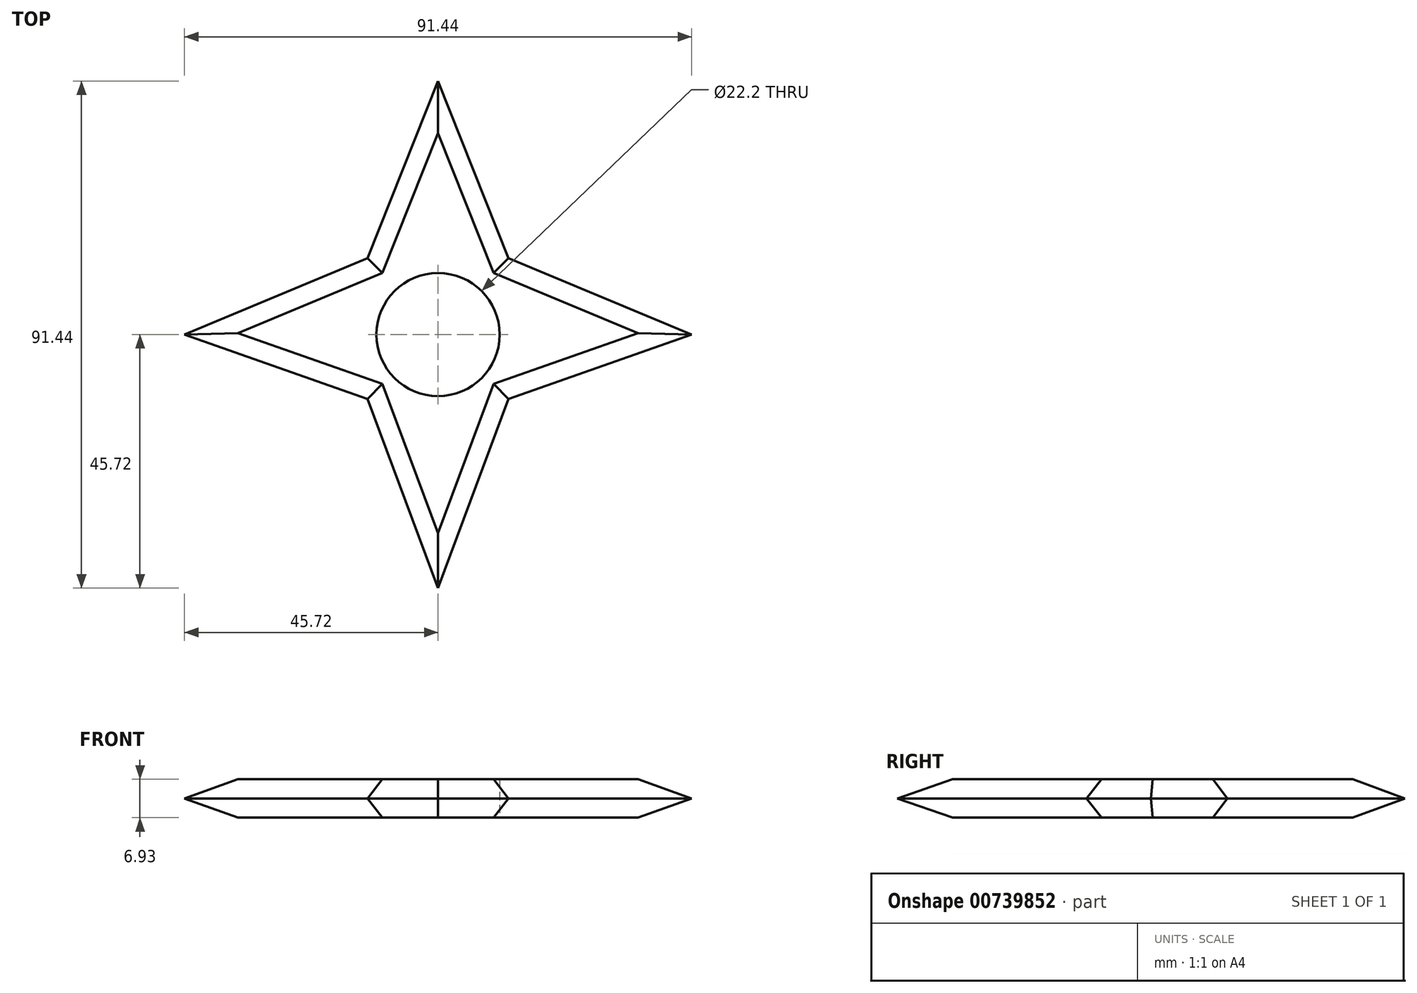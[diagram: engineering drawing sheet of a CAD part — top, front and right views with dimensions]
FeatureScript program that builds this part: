
annotation { "Feature Type Name" : "Feature", "Feature Type Description" : "" }
export const myFeature = defineFeature(function(context is Context, id is Id, definition is map)
    precondition{}
    {
        {
            var Q0;
            Q0=qCreatedBy(makeId("Top.planeOp"),FACE);
            var sketch = newSketch(context, id + "F0", { "sketchPlane" : qUnion([Q0])});
            skCircle(sketch, "E0", {"center": v(0, 0) * mm, "radius": 11.1 * mm});
            skLineSegment(sketch, "E1", {"start": v(0, 45.72) * mm, "end": v(-12.7, 13.75) * mm});
            skLineSegment(sketch, "E2", {"start": v(-12.7, 13.75) * mm, "end": v(-45.72, 0) * mm});
            skLineSegment(sketch, "E3", {"start": v(-45.72, 0) * mm, "end": v(-12.7, -11.65) * mm});
            skLineSegment(sketch, "E4", {"start": v(-12.7, -11.65) * mm, "end": v(0, -45.72) * mm});
            skLineSegment(sketch, "E5", {"start": v(0, -45.72) * mm, "end": v(12.7, -11.65) * mm});
            skLineSegment(sketch, "E6", {"start": v(12.7, -11.65) * mm, "end": v(45.72, 0) * mm});
            skLineSegment(sketch, "E7", {"start": v(45.72, 0) * mm, "end": v(12.7, 13.75) * mm});
            skLineSegment(sketch, "E8", {"start": v(12.7, 13.75) * mm, "end": v(0, 45.72) * mm});
            skSolve(sketch);
        }
        {
            var Q0;
            Q0=makeQuery(id+"F0.imprint","IMPRINT",FACE,{"disambiguationData":[TD([[makeQuery(id+"F0.imprint","IMPRINT",EDGE,{"derivedFrom":sQuery(id+"F0.wireOp",EDGE,"E0")}),-1.0]])]});
            extrude(context, id + "F1", {"entities" : qUnion([Q0]), "depth" : 6.93 * mm, "offsetDistance" : 25.4 * mm});
        }
        {
            var Q0;
            Q0=makeQuery(id+"F1.opExtrude","CAP_EDGE",EDGE,{"disambiguationData":[OSD([sQuery(id+"F0.wireOp",EDGE,"E5")])],"isStart":false});
            var Q1;
            Q1=makeQuery(id+"F1.opExtrude","CAP_EDGE",EDGE,{"disambiguationData":[OSD([sQuery(id+"F0.wireOp",EDGE,"E6")])],"isStart":false});
            var Q2;
            Q2=makeQuery(id+"F1.opExtrude","CAP_EDGE",EDGE,{"disambiguationData":[OSD([sQuery(id+"F0.wireOp",EDGE,"E3")])],"isStart":false});
            var Q3;
            Q3=makeQuery(id+"F1.opExtrude","CAP_EDGE",EDGE,{"disambiguationData":[OSD([sQuery(id+"F0.wireOp",EDGE,"E1")])],"isStart":false});
            var Q4;
            Q4=makeQuery(id+"F1.opExtrude","CAP_EDGE",EDGE,{"disambiguationData":[OSD([sQuery(id+"F0.wireOp",EDGE,"E2")])],"isStart":false});
            var Q5;
            Q5=makeQuery(id+"F1.opExtrude","CAP_EDGE",EDGE,{"disambiguationData":[OSD([sQuery(id+"F0.wireOp",EDGE,"E8")])],"isStart":false});
            var Q6;
            Q6=makeQuery(id+"F1.opExtrude","CAP_EDGE",EDGE,{"disambiguationData":[OSD([sQuery(id+"F0.wireOp",EDGE,"E7")])],"isStart":false});
            var Q7;
            Q7=makeQuery(id+"F1.opExtrude","CAP_EDGE",EDGE,{"disambiguationData":[OSD([sQuery(id+"F0.wireOp",EDGE,"E4")])],"isStart":false});
            chamfer(context, id + "F2", {"entities" : qUnion([Q0, Q1, Q2, Q3, Q4, Q5, Q6, Q7]), "width" : 3.47 * mm, "tangentPropagation" : true});
        }
        {
            var Q0;
            Q0=makeQuery(id+"F1.opExtrude","CAP_EDGE",EDGE,{"disambiguationData":[OSD([sQuery(id+"F0.wireOp",EDGE,"E5")])],"isStart":true});
            var Q1;
            Q1=makeQuery(id+"F1.opExtrude","CAP_EDGE",EDGE,{"disambiguationData":[OSD([sQuery(id+"F0.wireOp",EDGE,"E6")])],"isStart":true});
            var Q2;
            Q2=makeQuery(id+"F1.opExtrude","CAP_EDGE",EDGE,{"disambiguationData":[OSD([sQuery(id+"F0.wireOp",EDGE,"E3")])],"isStart":true});
            var Q3;
            Q3=makeQuery(id+"F1.opExtrude","CAP_EDGE",EDGE,{"disambiguationData":[OSD([sQuery(id+"F0.wireOp",EDGE,"E4")])],"isStart":true});
            var Q4;
            Q4=makeQuery(id+"F1.opExtrude","CAP_EDGE",EDGE,{"disambiguationData":[OSD([sQuery(id+"F0.wireOp",EDGE,"E8")])],"isStart":true});
            var Q5;
            Q5=makeQuery(id+"F1.opExtrude","CAP_EDGE",EDGE,{"disambiguationData":[OSD([sQuery(id+"F0.wireOp",EDGE,"E7")])],"isStart":true});
            var Q6;
            Q6=makeQuery(id+"F1.opExtrude","CAP_EDGE",EDGE,{"disambiguationData":[OSD([sQuery(id+"F0.wireOp",EDGE,"E2")])],"isStart":true});
            var Q7;
            Q7=makeQuery(id+"F1.opExtrude","CAP_EDGE",EDGE,{"disambiguationData":[OSD([sQuery(id+"F0.wireOp",EDGE,"E1")])],"isStart":true});
            chamfer(context, id + "F3", {"entities" : qUnion([Q0, Q1, Q2, Q3, Q4, Q5, Q6, Q7]), "width" : 3.47 * mm, "tangentPropagation" : true});
        }
    });
